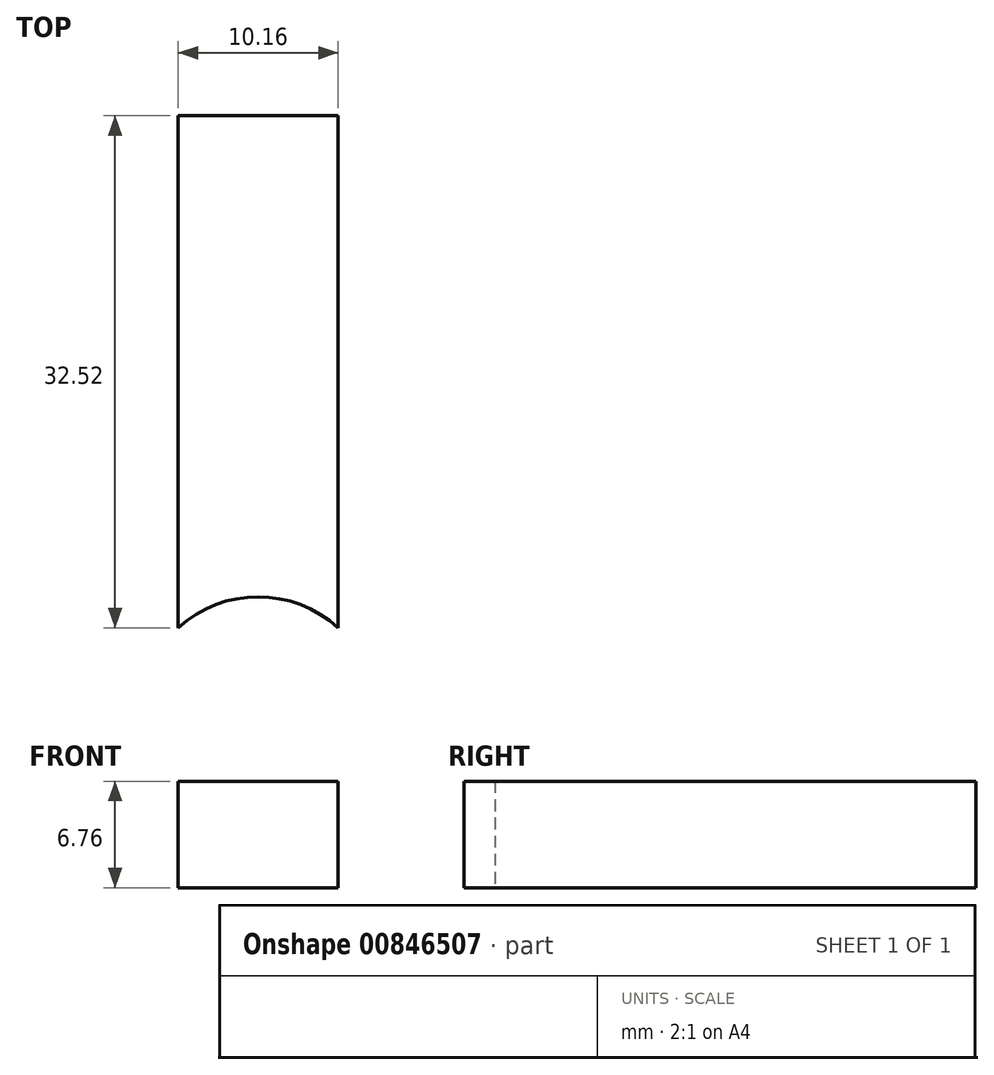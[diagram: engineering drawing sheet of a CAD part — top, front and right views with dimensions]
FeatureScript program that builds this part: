
annotation { "Feature Type Name" : "Feature", "Feature Type Description" : "" }
export const myFeature = defineFeature(function(context is Context, id is Id, definition is map)
    precondition{}
    {
        {
            var Q0;
            Q0=qCreatedBy(makeId("Top.planeOp"),FACE);
            var sketch = newSketch(context, id + "F0", { "sketchPlane" : qUnion([Q0])});
            skArc(sketch, "E0", {"start": v(5.08, 5.58) * mm, "mid": v(0, 7.54) * mm, "end": v(-5.08, 5.58) * mm});
            skLineSegment(sketch, "E1.top", {"start": v(-5.08, 38.1) * mm, "end": v(5.08, 38.1) * mm});
            skLineSegment(sketch, "E1.left", {"start": v(-5.08, 5.58) * mm, "end": v(-5.08, 38.1) * mm});
            skLineSegment(sketch, "E1.right", {"start": v(5.08, 5.58) * mm, "end": v(5.08, 38.1) * mm});
            skSolve(sketch);
        }
        {
            var Q0;
            Q0=makeQuery(id+"F0.imprint","IMPRINT",FACE,{"disambiguationData":[TD([[makeQuery(id+"F0.imprint","IMPRINT",EDGE,{"derivedFrom":sQuery(id+"F0.wireOp",EDGE,"E0")}),-1.0]])]});
            extrude(context, id + "F1", {"entities" : qUnion([Q0]), "depth" : 6.76 * mm, "offsetDistance" : 25.4 * mm});
        }
    });
